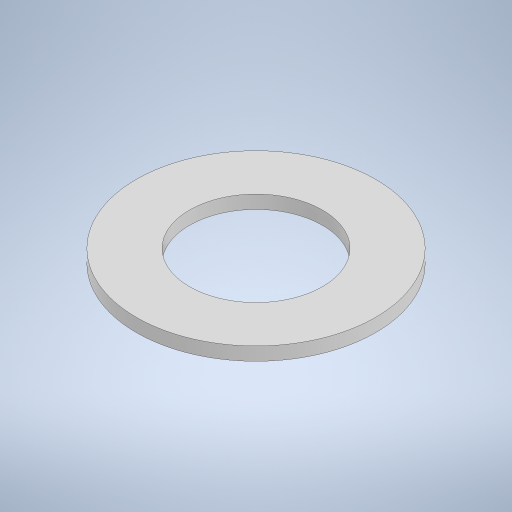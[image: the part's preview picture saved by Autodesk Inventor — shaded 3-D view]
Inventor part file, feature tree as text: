
AUTODESK INVENTOR PART (.ipt)
format: ipt  version: 2023 (Build 270158000, 158)  size: 231,424 bytes
history: native  units: mm
features: extrude x1, sketch x1
ambient origin geometry x8: Origin, YZ Plane, XZ Plane, XY Plane, X Axis, Y Axis, Z Axis, Center Point
bodies: Solid1 (feature_tree)
feature tree (2):
  extrude  "Extrusion1"  Depth=1.0mm
  sketch  "Sketch1"  dims[d0=10.0mm d1=18.0mm d2=1.0mm d3=0.0mm]
